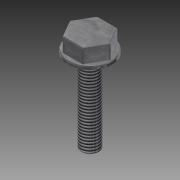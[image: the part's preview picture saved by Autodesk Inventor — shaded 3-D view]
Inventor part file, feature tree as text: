
AUTODESK INVENTOR PART (.ipt)
format: ipt  version: 2015 (Build 190159000, 159)  size: 132,608 bytes
history: native  units: mm
features: extrude x3, sketch x3, thread x1, chamfer x1, fillet x1
ambient origin geometry x8: Origin, YZ Plane, XZ Plane, XY Plane, X Axis, Y Axis, Z Axis, Center Point
bodies: 实体1 (feature_tree)
feature tree (9):
  extrude  "拉伸1"  Depth=1.5mm TaperAngle=0.0deg
  extrude  "拉伸2"  Depth=16.0mm
  extrude  "拉伸3"  Depth=8.0mm
  thread  "螺纹1"  [1 undecoded]
  chamfer  "倒角1"  Distance=10.0mm
  fillet  "圆角1"  Radius=0.5mm
  sketch  "草图1"  dims[d0=20.0mm d1=1.5mm d2=0.0mm]
  sketch  "草图2"  dims[d3=1.121996mm d4=16.0mm]
  sketch  "草图3"  dims[d5=6.5mm d6=0.0mm d7=8.0mm d8=38.0mm d9=0.0mm d10=10.0mm d11=0.0mm d12=0.5mm d13=2.0mm d14=45.0deg d15=0.5mm]
note: 1 required parameter value undecoded (feature->parameter linkage not recoverable at this tier; creation-order binding heuristic only, values carry confidence <= 0.55)
